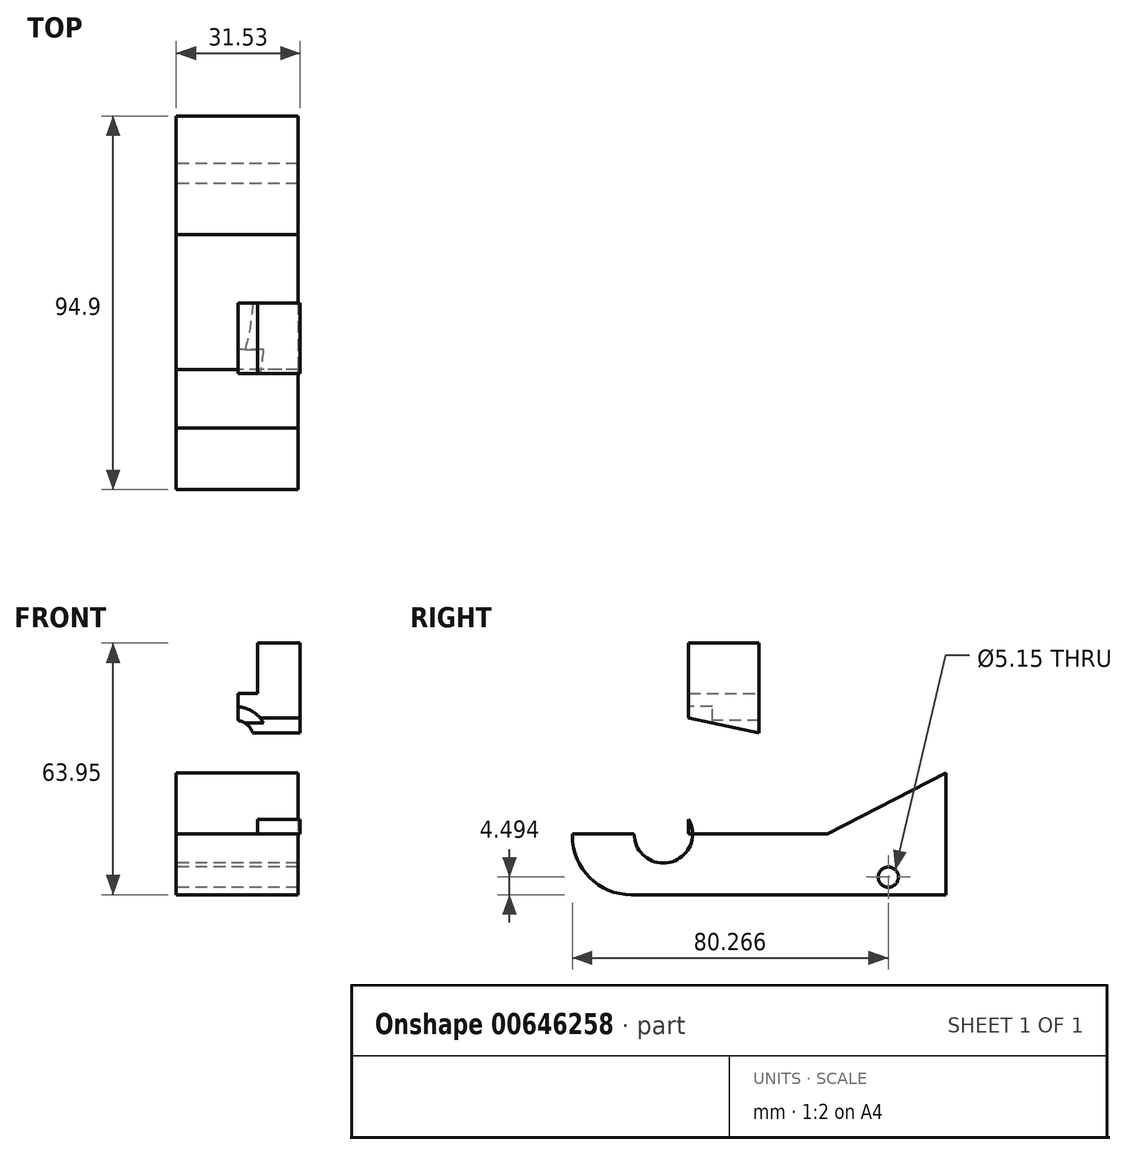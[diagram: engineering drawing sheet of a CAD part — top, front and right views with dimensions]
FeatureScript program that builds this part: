
annotation { "Feature Type Name" : "Feature", "Feature Type Description" : "" }
export const myFeature = defineFeature(function(context is Context, id is Id, definition is map)
    precondition{}
    {
        {
            var Q0;
            Q0=qCreatedBy(makeId("Front.planeOp"),FACE);
            var sketch = newSketch(context, id + "F0", { "sketchPlane" : qUnion([Q0])});
            skLineSegment(sketch, "E0", {"start": v(0, 0) * mm, "end": v(10.72, 0) * mm});
            skLineSegment(sketch, "E1", {"start": v(10.72, 0) * mm, "end": v(10.72, 12.74) * mm});
            skLineSegment(sketch, "E2", {"start": v(10.72, 12.74) * mm, "end": v(20.66, 12.74) * mm});
            skLineSegment(sketch, "E3", {"start": v(20.66, 12.74) * mm, "end": v(20.66, 0) * mm});
            skLineSegment(sketch, "E4", {"start": v(20.66, 0) * mm, "end": v(31.53, 0) * mm});
            skLineSegment(sketch, "E5", {"start": v(31.53, 0) * mm, "end": v(31.53, 24.23) * mm});
            skLineSegment(sketch, "E6", {"start": v(31.53, 24.23) * mm, "end": v(0, 24.23) * mm});
            skLineSegment(sketch, "E7", {"start": v(0, 24.23) * mm, "end": v(0, 0) * mm});
            skLineSegment(sketch, "E8.MirrorCS", {"start": v(10.72, 48.46) * mm, "end": v(10.72, 35.72) * mm});
            skLineSegment(sketch, "E9.MirrorCS", {"start": v(0, 48.46) * mm, "end": v(10.72, 48.46) * mm});
            skLineSegment(sketch, "E10.MirrorCS", {"start": v(0, 24.23) * mm, "end": v(0, 48.46) * mm});
            skLineSegment(sketch, "E11.MirrorCS", {"start": v(10.72, 35.72) * mm, "end": v(20.66, 35.72) * mm});
            skLineSegment(sketch, "E12.MirrorCS", {"start": v(20.66, 35.72) * mm, "end": v(20.66, 48.46) * mm});
            skLineSegment(sketch, "E13.MirrorCS", {"start": v(20.66, 48.46) * mm, "end": v(31.53, 48.46) * mm});
            skLineSegment(sketch, "E14.MirrorCS", {"start": v(31.53, 48.46) * mm, "end": v(31.53, 24.23) * mm});
            skSolve(sketch);
        }
        {
            var Q0;
            Q0=makeQuery(id+"F0.imprint","IMPRINT",FACE,{"disambiguationData":[TD([[makeQuery(id+"F0.imprint","IMPRINT",EDGE,{"derivedFrom":sQuery(id+"F0.wireOp",EDGE,"E6")}),-1.0]])]});
            var Q1;
            Q1=makeQuery(id+"F0.imprint","IMPRINT",FACE,{"disambiguationData":[TD([[makeQuery(id+"F0.imprint","IMPRINT",EDGE,{"derivedFrom":sQuery(id+"F0.wireOp",EDGE,"E0")}),1.0]])]});
            extrude(context, id + "F1", {"entities" : qUnion([Q0, Q1]), "depth" : 17.9 * mm, "offsetDistance" : 25 * mm});
        }
        {
            var Q0;
            Q0=makeQuery(id+"F1.opExtrude","CAP_FACE",FACE,{"disambiguationData":[OSD([sQuery(id+"F0.wireOp",EDGE,"E0"),sQuery(id+"F0.wireOp",EDGE,"E1"),sQuery(id+"F0.wireOp",EDGE,"E2"),sQuery(id+"F0.wireOp",EDGE,"E3"),sQuery(id+"F0.wireOp",EDGE,"E4"),sQuery(id+"F0.wireOp",EDGE,"E5"),sQuery(id+"F0.wireOp",EDGE,"E7"),sQuery(id+"F0.wireOp",EDGE,"E9.MirrorCS"),sQuery(id+"F0.wireOp",EDGE,"E10.MirrorCS"),sQuery(id+"F0.wireOp",EDGE,"E8.MirrorCS"),sQuery(id+"F0.wireOp",EDGE,"E11.MirrorCS"),sQuery(id+"F0.wireOp",EDGE,"E12.MirrorCS"),sQuery(id+"F0.wireOp",EDGE,"E13.MirrorCS"),sQuery(id+"F0.wireOp",EDGE,"E14.MirrorCS")])],"isStart":false});
            var sketch = newSketch(context, id + "F2", { "sketchPlane" : qUnion([Q0])});
            skCircle(sketch, "E15", {"center": v(15.1, 24.3) * mm, "radius": 4.53 * mm});
            skSolve(sketch);
        }
        {
            var Q0;
            Q0 = qSketchRegion(id + "F2", true);
            extrude(context, id + "F3", {"entities" : qUnion([Q0]), "operationType" : NewBodyOperationType.REMOVE, "oppositeDirection" : true, "depth" : 25 * mm, "offsetDistance" : 25 * mm});
        }
        {
            var Q0;
            Q0=makeQuery(id+"F1.opExtrude","CAP_FACE",FACE,{"disambiguationData":[OSD([sQuery(id+"F0.wireOp",EDGE,"E0"),sQuery(id+"F0.wireOp",EDGE,"E1"),sQuery(id+"F0.wireOp",EDGE,"E2"),sQuery(id+"F0.wireOp",EDGE,"E3"),sQuery(id+"F0.wireOp",EDGE,"E4"),sQuery(id+"F0.wireOp",EDGE,"E5"),sQuery(id+"F0.wireOp",EDGE,"E7"),sQuery(id+"F0.wireOp",EDGE,"E9.MirrorCS"),sQuery(id+"F0.wireOp",EDGE,"E10.MirrorCS"),sQuery(id+"F0.wireOp",EDGE,"E8.MirrorCS"),sQuery(id+"F0.wireOp",EDGE,"E11.MirrorCS"),sQuery(id+"F0.wireOp",EDGE,"E12.MirrorCS"),sQuery(id+"F0.wireOp",EDGE,"E13.MirrorCS"),sQuery(id+"F0.wireOp",EDGE,"E14.MirrorCS")])],"isStart":false});
            var sketch = newSketch(context, id + "F4", { "sketchPlane" : qUnion([Q0])});
            skCircle(sketch, "E16", {"center": v(15.1, 24.3) * mm, "radius": 8.04 * mm});
            skSolve(sketch);
        }
        {
            var Q0;
            Q0 = qSketchRegion(id + "F4", true);
            extrude(context, id + "F5", {"entities" : qUnion([Q0]), "operationType" : NewBodyOperationType.REMOVE, "oppositeDirection" : true, "depth" : 6 * mm, "offsetDistance" : 25 * mm});
        }
        {
            var Q0;
            Q0=makeQuery(id+"F1.opExtrude","CAP_FACE",FACE,{"disambiguationData":[OSD([sQuery(id+"F0.wireOp",EDGE,"E0"),sQuery(id+"F0.wireOp",EDGE,"E1"),sQuery(id+"F0.wireOp",EDGE,"E2"),sQuery(id+"F0.wireOp",EDGE,"E3"),sQuery(id+"F0.wireOp",EDGE,"E4"),sQuery(id+"F0.wireOp",EDGE,"E5"),sQuery(id+"F0.wireOp",EDGE,"E7"),sQuery(id+"F0.wireOp",EDGE,"E9.MirrorCS"),sQuery(id+"F0.wireOp",EDGE,"E10.MirrorCS"),sQuery(id+"F0.wireOp",EDGE,"E8.MirrorCS"),sQuery(id+"F0.wireOp",EDGE,"E11.MirrorCS"),sQuery(id+"F0.wireOp",EDGE,"E12.MirrorCS"),sQuery(id+"F0.wireOp",EDGE,"E13.MirrorCS"),sQuery(id+"F0.wireOp",EDGE,"E14.MirrorCS")])],"isStart":false});
            var sketch = newSketch(context, id + "F6", { "sketchPlane" : qUnion([Q0])});
            skLineSegment(sketch, "E17.bottom", {"start": v(15.69, 35.72) * mm, "end": v(0, 35.72) * mm});
            skLineSegment(sketch, "E17.top", {"start": v(15.69, 0) * mm, "end": v(0, 0) * mm});
            skLineSegment(sketch, "E17.left", {"start": v(15.69, 35.72) * mm, "end": v(15.69, 0) * mm});
            skLineSegment(sketch, "E17.right", {"start": v(0, 35.72) * mm, "end": v(0, 0) * mm});
            skLineSegment(sketch, "E18.top", {"start": v(15.69, 52.5) * mm, "end": v(0, 52.5) * mm});
            skLineSegment(sketch, "E18.left", {"start": v(15.69, 35.72) * mm, "end": v(15.69, 52.5) * mm});
            skLineSegment(sketch, "E18.right", {"start": v(0, 35.72) * mm, "end": v(0, 52.5) * mm});
            skSolve(sketch);
        }
        {
            var Q0;
            {var subQ1=sQuery(id+"F6.wireOp",EDGE,"E18.top");Q0=makeQuery(id+"F6.imprint","IMPRINT",FACE,{"disambiguationData":[TD([[makeQuery(id+"F6.imprint","IMPRINT",EDGE,{"derivedFrom":subQ1}),1.0]])]});}
            var Q1;
            {var subQ1=makeQuery(id+"F1.opExtrude","CAP_EDGE",EDGE,{"disambiguationData":[OSD([sQuery(id+"F0.wireOp",EDGE,"E1")])],"isStart":false});Q1=makeQuery(id+"F6.imprint","IMPRINT",FACE,{"disambiguationData":[TD([[makeQuery(id+"F6.imprint","IMPRINT",EDGE,{"derivedFrom":subQ1}),-1.0]])]});}
            var Q2;
            {var subQ9=sQuery(id+"F6.wireOp",EDGE,"E17.right");Q2=makeQuery(id+"F6.imprint","IMPRINT",FACE,{"disambiguationData":[TD([[makeQuery(id+"F6.imprint","IMPRINT",EDGE,{"derivedFrom":subQ9}),-1.0]])]});}
            var Q3;
            {var subQ0=sQuery(id+"F6.wireOp",EDGE,"E17.left");var subQ1=makeQuery(id+"F5.boolean.opBoolean","COPY",EDGE,{"derivedFrom":makeQuery(id+"F5.opExtrude","CAP_EDGE",EDGE,{"disambiguationData":[OSD([sQuery(id+"F4.wireOp",EDGE,"E16")])],"isStart":true})});var subQ2=makeQuery(id+"F6.imprint","INTERSECT",VERTEX,{"disambiguationData":[OD(0.0)],"derivedFrom":[subQ1,subQ0]});Q3=makeQuery(id+"F6.imprint","IMPRINT",FACE,{"disambiguationData":[TD([[makeQuery(id+"F6.imprint","IMPRINT",EDGE,{"disambiguationData":[TD([[subQ2,-1.0]])],"derivedFrom":subQ0}),-1.0]])]});}
            var Q4;
            {var subQ4=makeQuery(id+"F1.opExtrude","CAP_EDGE",EDGE,{"disambiguationData":[OSD([sQuery(id+"F0.wireOp",EDGE,"E9.MirrorCS")])],"isStart":false});Q4=makeQuery(id+"F6.imprint","IMPRINT",FACE,{"disambiguationData":[TD([[makeQuery(id+"F6.imprint","IMPRINT",EDGE,{"derivedFrom":subQ4}),-1.0]])]});}
            extrude(context, id + "F7", {"entities" : qUnion([Q0, Q1, Q2, Q3, Q4]), "operationType" : NewBodyOperationType.REMOVE, "oppositeDirection" : true, "depth" : 25 * mm, "offsetDistance" : 25 * mm});
        }
        {
            var Q0;
            Q0=qCreatedBy(makeId("Right.planeOp"),FACE);
            var sketch = newSketch(context, id + "F8", { "sketchPlane" : qUnion([Q0])});
            skLineSegment(sketch, "E19.bottom", {"start": v(-32.45, 15.49) * mm, "end": v(47.45, 15.49) * mm});
            skLineSegment(sketch, "E19.top", {"start": v(-32.45, -15.49) * mm, "end": v(47.45, -15.49) * mm});
            skLineSegment(sketch, "E19.left", {"start": v(-47.45, 0.49) * mm, "end": v(-47.45, -0.49) * mm});
            skLineSegment(sketch, "E19.right", {"start": v(47.45, 15.49) * mm, "end": v(47.45, -15.49) * mm});
            skPoint(sketch, "E19.middle", {"position": v(0, 0) * mm});
            skPoint(sketch, "E20.visualSharp", {"position": v(-47.45, 15.49) * mm});
            skArc(sketch, "E20.filletArc", {"start": v(-32.45, 15.49) * mm, "mid": v(-43.06, 11.1) * mm, "end": v(-47.45, 0.49) * mm});
            skPoint(sketch, "E21.visualSharp", {"position": v(-47.45, -15.49) * mm});
            skArc(sketch, "E21.filletArc", {"start": v(-47.45, -0.49) * mm, "mid": v(-43.06, -11.1) * mm, "end": v(-32.45, -15.49) * mm});
            skCircle(sketch, "E22", {"center": v(32.82, 11) * mm, "radius": 2.57 * mm});
            skCircle(sketch, "E23.MirrorC", {"center": v(32.82, -11) * mm, "radius": 2.57 * mm});
            skCircle(sketch, "E24", {"center": v(-24.33, 0) * mm, "radius": 7.42 * mm});
            skPoint(sketch, "E24.centerSnap0", {"position": v(47.45, 0) * mm});
            skSolve(sketch);
        }
        {
            var Q0;
            Q0 = qSketchRegion(id + "F8", true);
            extrude(context, id + "F9", {"entities" : qUnion([Q0]), "depth" : 30.9 * mm, "offsetDistance" : 25 * mm});
        }
        {
            var Q0;
            Q0=makeQuery(id+"F9.opExtrude","CAP_FACE",FACE,{"disambiguationData":[OSD([sQuery(id+"F8.wireOp",EDGE,"E19.bottom"),sQuery(id+"F8.wireOp",EDGE,"E19.top"),sQuery(id+"F8.wireOp",EDGE,"E19.left"),sQuery(id+"F8.wireOp",EDGE,"E19.right"),sQuery(id+"F8.wireOp",EDGE,"E20.filletArc"),sQuery(id+"F8.wireOp",EDGE,"E21.filletArc"),sQuery(id+"F8.wireOp",EDGE,"E22"),sQuery(id+"F8.wireOp",EDGE,"E23.MirrorC"),sQuery(id+"F8.wireOp",EDGE,"E24")])],"isStart":true});
            var sketch = newSketch(context, id + "F10", { "sketchPlane" : qUnion([Q0])});
            skLineSegment(sketch, "E25", {"start": v(57.62, 0) * mm, "end": v(-17.38, 0) * mm});
            skLineSegment(sketch, "E26", {"start": v(-17.38, 0) * mm, "end": v(-47.45, 15.49) * mm});
            skLineSegment(sketch, "E27", {"start": v(-47.45, 15.49) * mm, "end": v(25.23, 31.04) * mm});
            skLineSegment(sketch, "E28", {"start": v(25.23, 31.04) * mm, "end": v(61.22, 12.67) * mm});
            skLineSegment(sketch, "E29", {"start": v(61.22, 12.67) * mm, "end": v(57.62, 0) * mm});
            skSolve(sketch);
        }
        {
            var Q0;
            Q0=makeQuery(id+"F10.imprint","IMPRINT",FACE,{"disambiguationData":[TD([[makeQuery(id+"F10.imprint","IMPRINT",EDGE,{"derivedFrom":sQuery(id+"F10.wireOp",EDGE,"E27")}),-1.0]])]});
            var Q1;
            {var subQ0=sQuery(id+"F10.wireOp",EDGE,"E26");Q1=makeQuery(id+"F10.imprint","IMPRINT",FACE,{"disambiguationData":[TD([[makeQuery(id+"F10.imprint","IMPRINT",EDGE,{"derivedFrom":subQ0}),-1.0]])]});}
            extrude(context, id + "F11", {"entities" : qUnion([Q0, Q1]), "operationType" : NewBodyOperationType.REMOVE, "oppositeDirection" : true, "depth" : 46.3 * mm, "offsetDistance" : 25 * mm});
        }
    });
